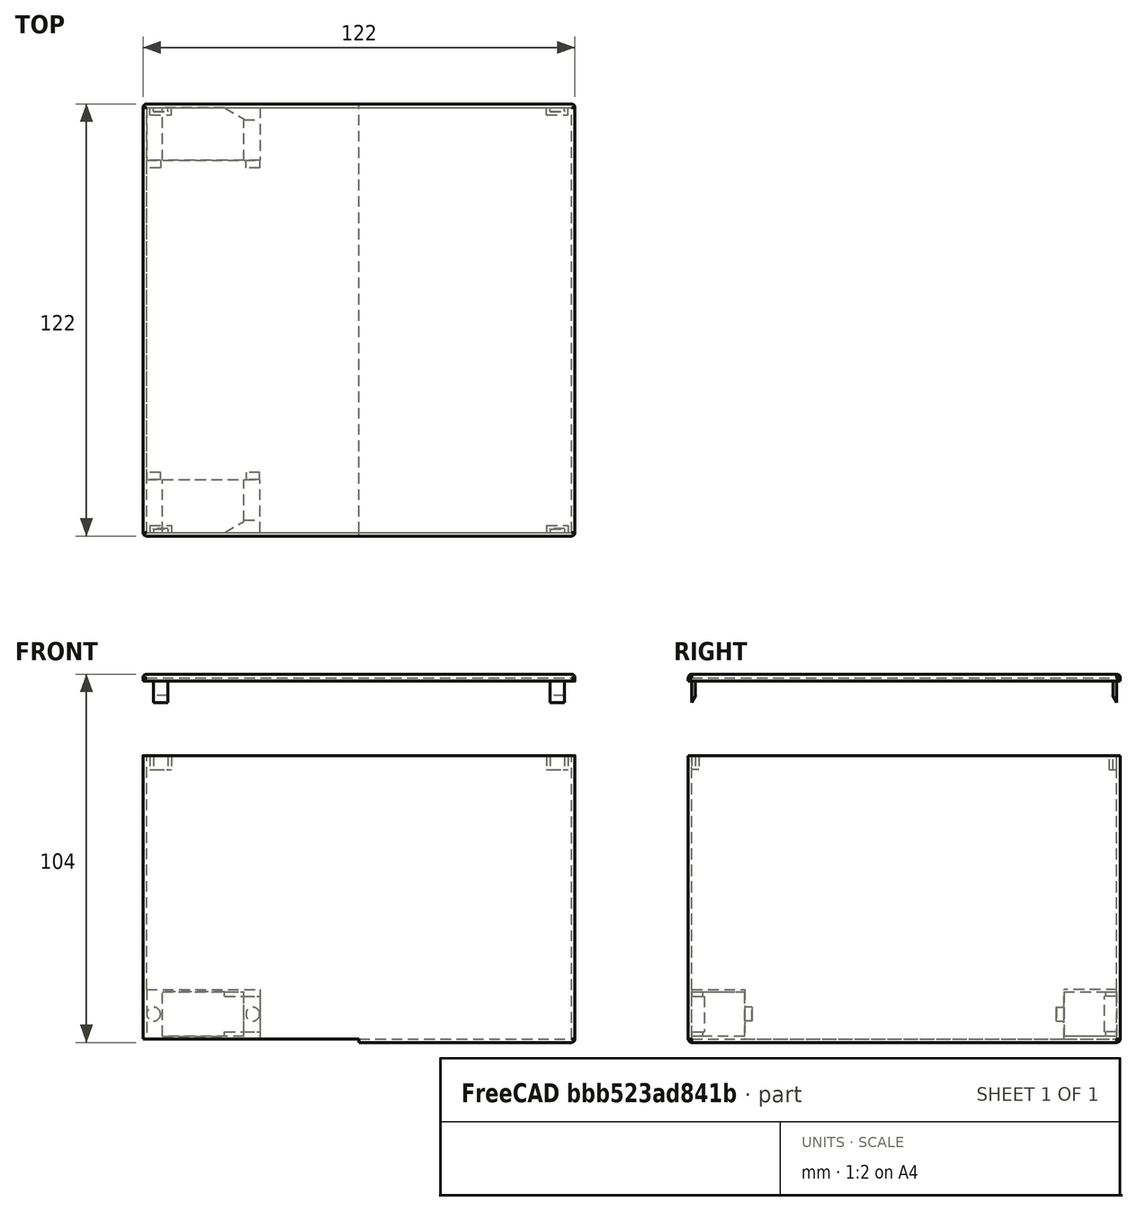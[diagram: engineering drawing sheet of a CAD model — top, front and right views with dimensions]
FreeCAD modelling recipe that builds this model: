
FCSTD DOCUMENT  (FreeCAD 0.21R33771 (Git))
Label: body draft
License: All rights reserved
LicenseURL: https://en.wikipedia.org/wiki/All_rights_reserved
objects: Part::Box×28, Part::Cut×13, Part::MultiFuse×9, Part::Cylinder×4, Part::Thickness×2, Part::Feature×2, Part::MultiCommon×1
note: 59 computed .brp shape members not serialized (recipe doc carries the construction recipe); baked Part::Feature solids carry a one-line shape summary decoded from their .brp

FEATURE [Part::Box] Box003  label="Cube058"
  AttacherType = Attacher::AttachEngine3D
  Height = 80
  Length = 120
  Placement = pos=(0,0,155) rot=(0,0,1;0rad)
  Width = 120
FEATURE [Part::Box] Box078  label="Cube059"
  AttacherType = Attacher::AttachEngine3D
  Height = 14.9
  Length = 32
  Width = 14
FEATURE [Part::Box] Box079  label="Cube060"
  AttacherType = Attacher::AttachEngine3D
  Height = 3.5
  Length = 10
  Placement = pos=(22,2,0) rot=(0,0,1;0rad)
  Width = 10
FEATURE [Part::Box] Box080  label="Cube061"
  AttacherType = Attacher::AttachEngine3D
  Height = 14.9
  Length = 32
  Width = 14
FEATURE [Part::Box] Box081  label="Cube062"
  AttacherType = Attacher::AttachEngine3D
  Height = 3.5
  Length = 10
  Placement = pos=(22,2,0) rot=(0,0,1;0rad)
  Width = 10
FEATURE [Part::Box] Box082  label="Cube063"
  AttacherType = Attacher::AttachEngine3D
  Height = 2
  Length = 122
  Placement = pos=(-1,-1,234) rot=(0,0,1;0rad)
  Width = 122
FEATURE [Part::Box] Box083  label="Cube064"
  AttacherType = Attacher::AttachEngine3D
  Height = 80
  Length = 120
  Placement = pos=(0,0,155) rot=(0,0,1;0rad)
  Width = 120
FEATURE [Part::Box] Box084  label="Cube065"
  AttacherType = Attacher::AttachEngine3D
  Height = 1
  Length = 61
  Placement = pos=(-1,-1,154) rot=(0,0,1;0rad)
  Width = 122
FEATURE [Part::Box] Box085  label="Cube066"
  AttacherType = Attacher::AttachEngine3D
  Height = 6
  Length = 2
  Width = 4
FEATURE [Part::Box] Box086  label="Cube067"
  AttacherType = Attacher::AttachEngine3D
  Height = 4
  Length = 1
  Placement = pos=(1,0,1) rot=(0,0,1;0rad)
  Width = 4
FEATURE [Part::Box] Box087  label="Cube068"
  AttacherType = Attacher::AttachEngine3D
  Height = 6
  Length = 2
  Width = 4
FEATURE [Part::Box] Box088  label="Cube069"
  AttacherType = Attacher::AttachEngine3D
  Height = 4
  Length = 1
  Placement = pos=(1,0,1) rot=(0,0,1;0rad)
  Width = 4
FEATURE [Part::Box] Box089  label="Cube070"
  AttacherType = Attacher::AttachEngine3D
  Height = 6
  Length = 2
  Width = 4
FEATURE [Part::Box] Box090  label="Cube071"
  AttacherType = Attacher::AttachEngine3D
  Height = 4
  Length = 1
  Placement = pos=(1,0,1) rot=(0,0,1;0rad)
  Width = 4
FEATURE [Part::Box] Box091  label="Cube072"
  AttacherType = Attacher::AttachEngine3D
  Height = 6
  Length = 2
  Width = 4
FEATURE [Part::Box] Box092  label="Cube073"
  AttacherType = Attacher::AttachEngine3D
  Height = 4
  Length = 1
  Placement = pos=(1,0,1) rot=(0,0,1;0rad)
  Width = 4
FEATURE [Part::Box] Box093  label="Cube074"
  AttacherType = Attacher::AttachEngine3D
  Height = 4
  Length = 2
  Placement = pos=(1,0,1) rot=(0,0,-1;0.523599rad)
  Width = 3
FEATURE [Part::Box] Box094  label="Cube075"
  AttacherType = Attacher::AttachEngine3D
  Height = 4
  Length = 1
  Placement = pos=(1,0,1) rot=(0,0,1;0rad)
  Width = 6
FEATURE [Part::Box] Box095  label="Cube076"
  AttacherType = Attacher::AttachEngine3D
  Height = 4
  Length = 1.2
  Placement = pos=(1,0,1) rot=(0,0,1;0rad)
  Width = 2
FEATURE [Part::Box] Box096  label="Cube077"
  AttacherType = Attacher::AttachEngine3D
  Height = 4
  Length = 2
  Placement = pos=(1,0,1) rot=(0,0,-1;0.523599rad)
  Width = 3
FEATURE [Part::Box] Box097  label="Cube078"
  AttacherType = Attacher::AttachEngine3D
  Height = 4
  Length = 1
  Placement = pos=(1,0,1) rot=(0,0,1;0rad)
  Width = 6
FEATURE [Part::Box] Box098  label="Cube079"
  AttacherType = Attacher::AttachEngine3D
  Height = 4
  Length = 1.2
  Placement = pos=(1,0,1) rot=(0,0,1;0rad)
  Width = 2
FEATURE [Part::Box] Box099  label="Cube080"
  AttacherType = Attacher::AttachEngine3D
  Height = 4
  Length = 2
  Placement = pos=(1,0,1) rot=(0,0,-1;0.523599rad)
  Width = 3
FEATURE [Part::Box] Box100  label="Cube081"
  AttacherType = Attacher::AttachEngine3D
  Height = 4
  Length = 1
  Placement = pos=(1,0,1) rot=(0,0,1;0rad)
  Width = 6
FEATURE [Part::Box] Box101  label="Cube082"
  AttacherType = Attacher::AttachEngine3D
  Height = 4
  Length = 1.2
  Placement = pos=(1,0,1) rot=(0,0,1;0rad)
  Width = 2
FEATURE [Part::Box] Box102  label="Cube083"
  AttacherType = Attacher::AttachEngine3D
  Height = 4
  Length = 2
  Placement = pos=(1,0,1) rot=(0,0,-1;0.523599rad)
  Width = 3
FEATURE [Part::Box] Box103  label="Cube084"
  AttacherType = Attacher::AttachEngine3D
  Height = 4
  Length = 1
  Placement = pos=(1,0,1) rot=(0,0,1;0rad)
  Width = 6
FEATURE [Part::Box] Box104  label="Cube085"
  AttacherType = Attacher::AttachEngine3D
  Height = 4
  Length = 1.2
  Placement = pos=(1,0,1) rot=(0,0,1;0rad)
  Width = 2
FEATURE [Part::Cut] Cut037
  Base = -> Box085
  Placement = pos=(1,2,235) rot=(0.57735,-0.57735,0.57735;4.18879rad)
  Tool = -> Box086
FEATURE [Part::Cut] Cut038
  Base = -> Box087
  Placement = pos=(113,2,235) rot=(0.57735,-0.57735,0.57735;4.18879rad)
  Tool = -> Box088
FEATURE [Part::Cut] Cut039
  Base = -> Box089
  Placement = pos=(1,118,231) rot=(0.57735,0.57735,0.57735;2.0944rad)
  Tool = -> Box090
FEATURE [Part::Cut] Cut040
  Base = -> Box091
  Placement = pos=(113,118,231) rot=(0.57735,0.57735,0.57735;2.0944rad)
  Tool = -> Box092
FEATURE [Part::Cylinder] Cylinder016  label="Cylindre016"
  Angle = 360
  AttacherType = Attacher::AttachEngine3D
  FirstAngle = 0
  Height = 2.1
  Placement = pos=(2,7,14.9) rot=(0,0,1;0rad)
  Radius = 1.95
  SecondAngle = 0
FEATURE [Part::Cylinder] Cylinder017  label="Cylindre017"
  Angle = 360
  AttacherType = Attacher::AttachEngine3D
  FirstAngle = 0
  Height = 2.1
  Placement = pos=(30,7,14.9) rot=(0,0,1;0rad)
  Radius = 1.95
  SecondAngle = 0
FEATURE [Part::Cylinder] Cylinder018  label="Cylindre018"
  Angle = 360
  AttacherType = Attacher::AttachEngine3D
  FirstAngle = 0
  Height = 2.1
  Placement = pos=(2,7,14.9) rot=(0,0,1;0rad)
  Radius = 1.95
  SecondAngle = 0
FEATURE [Part::Cylinder] Cylinder019  label="Cylindre019"
  Angle = 360
  AttacherType = Attacher::AttachEngine3D
  FirstAngle = 0
  Height = 2.1
  Placement = pos=(30,7,14.9) rot=(0,0,1;0rad)
  Radius = 1.95
  SecondAngle = 0
FEATURE [Part::MultiFuse] Fusion030
  Shapes = -> [Box094,Box095]
FEATURE [Part::Cut] Cut041
  Base = -> Fusion030
  Placement = pos=(1,-1,250) rot=(0.57735,0.57735,0.57735;2.0944rad)
  Tool = -> Box093
FEATURE [Part::MultiFuse] Fusion031
  Shapes = -> [Box097,Box098]
FEATURE [Part::Cut] Cut042
  Base = -> Fusion031
  Placement = pos=(113,-1,250) rot=(0.57735,0.57735,0.57735;2.0944rad)
  Tool = -> Box096
FEATURE [Part::MultiFuse] Fusion032
  Shapes = -> [Box100,Box101]
FEATURE [Part::Cut] Cut043
  Base = -> Fusion032
  Placement = pos=(119,121,250) rot=(0.57735,-0.57735,-0.57735;2.0944rad)
  Tool = -> Box099
FEATURE [Part::MultiFuse] Fusion033
  Shapes = -> [Box103,Box104]
FEATURE [Part::Cut] Cut044
  Base = -> Fusion033
  Placement = pos=(7,121,250) rot=(0.57735,-0.57735,-0.57735;2.0944rad)
  Tool = -> Box102
FEATURE [Part::Thickness] Thickness010
  Faces = -> Box083 [Face5]
  Intersection = false
  Join = 0
  Mode = 0
  SelfIntersection = false
  Value = 1
FEATURE [Part::MultiCommon] Common002
  Placement = pos=(0,0,22) rot=(0,0,1;0rad)
  Shapes = -> [Thickness010,Box082]
FEATURE [Part::MultiFuse] Fusion034  label="panel"
  Shapes = -> [Common002,Cut041,Cut042,Cut043,Cut044]
FEATURE [Part::Thickness] Thickness011
  Faces = -> Box003 [Face6]
  Intersection = false
  Join = 0
  Mode = 0
  SelfIntersection = false
  Value = 1
FEATURE [Part::Cut] Cut036
  Base = -> Thickness011
  Tool = -> Box084
FEATURE [Part::MultiFuse] Fusion029
  Shapes = -> [Cut036,Cut037,Cut038,Cut039,Cut040]
FEATURE [Part::Feature] _g_servo002_solid009  label="9g_servo009"
  Placement = pos=(16,7,11) rot=(0,0,1;0rad)
  shape: bbox 32 x 12.5 x 29.27 mm, 117 faces (baked)
FEATURE [Part::Cut] Cut032
  Base = -> Box078
  Tool = -> _g_servo002_solid009
FEATURE [Part::MultiFuse] Fusion027
  Shapes = -> [Cut032,Cylinder016,Cylinder017]
FEATURE [Part::Cut] Cut033  label="ServoSocket007"
  Base = -> Fusion027
  Placement = pos=(0,-1.4e-14,169) rot=(-1,0,0;1.5708rad)
  Tool = -> Box079
FEATURE [Part::Feature] _g_servo002_solid010  label="9g_servo010"
  Placement = pos=(16,7,11) rot=(0,0,1;0rad)
  shape: bbox 32 x 12.5 x 29.27 mm, 117 faces (baked)
FEATURE [Part::Cut] Cut034
  Base = -> Box080
  Tool = -> _g_servo002_solid010
FEATURE [Part::MultiFuse] Fusion028
  Shapes = -> [Cut034,Cylinder018,Cylinder019]
FEATURE [Part::Cut] Cut035  label="ServoSocket008"
  Base = -> Fusion028
  Placement = pos=(0,120,155) rot=(1,0,0;1.5708rad)
  Tool = -> Box081
FEATURE [Part::MultiFuse] Fusion035  label="body"
  Shapes = -> [Fusion029,Cut033,Cut035]
